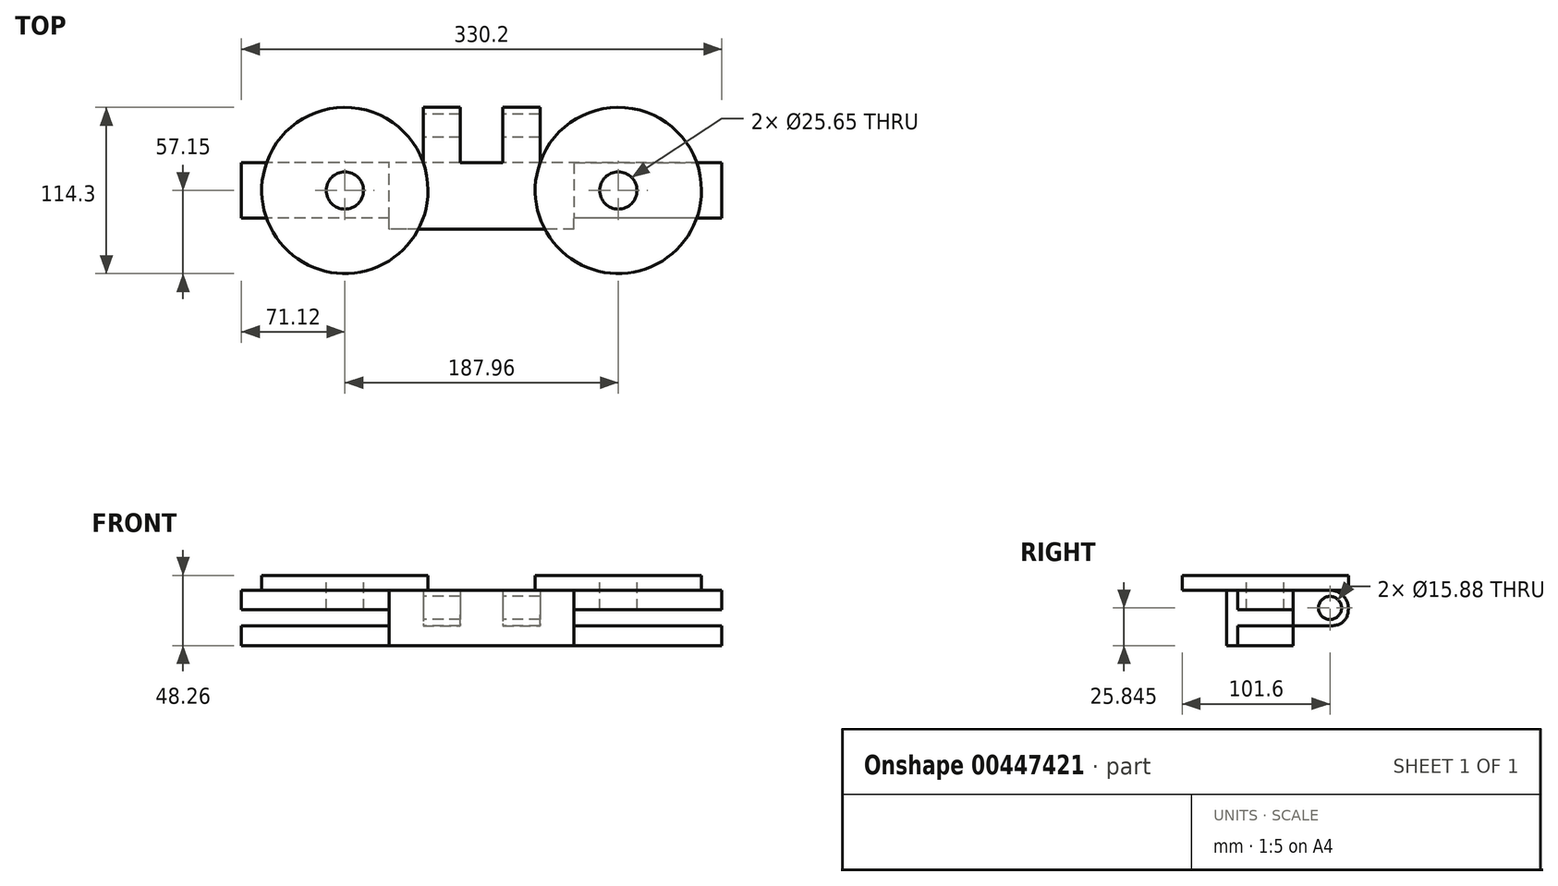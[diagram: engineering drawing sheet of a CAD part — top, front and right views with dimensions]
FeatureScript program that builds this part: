
annotation { "Feature Type Name" : "Feature", "Feature Type Description" : "" }
export const myFeature = defineFeature(function(context is Context, id is Id, definition is map)
    precondition{}
    {
        {
            var Q0;
            Q0=qCreatedBy(makeId("Top.planeOp"),FACE);
            var sketch = newSketch(context, id + "F0", { "sketchPlane" : qUnion([Q0])});
            skLineSegment(sketch, "E0.bottom", {"start": v(165.1, -19.05) * mm, "end": v(-165.1, -19.05) * mm});
            skLineSegment(sketch, "E0.top", {"start": v(165.1, 19.05) * mm, "end": v(-165.1, 19.05) * mm});
            skLineSegment(sketch, "E0.left", {"start": v(165.1, -19.05) * mm, "end": v(165.1, 19.05) * mm});
            skLineSegment(sketch, "E0.right", {"start": v(-165.1, -19.05) * mm, "end": v(-165.1, 19.05) * mm});
            skPoint(sketch, "E0.middle", {"position": v(0, 0) * mm});
            skSolve(sketch);
        }
        {
            var Q0;
            Q0=makeQuery(id+"F0.imprint","IMPRINT",FACE,{"disambiguationData":[TD([[makeQuery(id+"F0.imprint","IMPRINT",EDGE,{"derivedFrom":sQuery(id+"F0.wireOp",EDGE,"E0.bottom")}),-1.0]])]});
            extrude(context, id + "F1", {"entities" : qUnion([Q0]), "depth" : 38.1 * mm});
        }
        {
            var Q0;
            Q0=makeQuery(id+"F1.opExtrude","SWEPT_FACE",FACE,{"disambiguationData":[OSD([sQuery(id+"F0.wireOp",EDGE,"E0.right")])]});
            var sketch = newSketch(context, id + "F2", { "sketchPlane" : qUnion([Q0])});
            skLineSegment(sketch, "E1", {"start": v(0, 38.1) * mm, "end": v(0, 0) * mm});
            skPoint(sketch, "E2", {"position": v(0, 19.05) * mm});
            skLineSegment(sketch, "E3.bottom", {"start": v(19.05, 13.59) * mm, "end": v(-19.05, 13.59) * mm});
            skLineSegment(sketch, "E3.top", {"start": v(19.05, 24.51) * mm, "end": v(-19.05, 24.51) * mm});
            skLineSegment(sketch, "E3.left", {"start": v(19.05, 13.59) * mm, "end": v(19.05, 24.51) * mm});
            skLineSegment(sketch, "E3.right", {"start": v(-19.05, 13.59) * mm, "end": v(-19.05, 24.51) * mm});
            skSolve(sketch);
        }
        {
            var Q0;
            {var subQ5=sQuery(id+"F2.wireOp",EDGE,"E3.left");Q0=makeQuery(id+"F2.imprint","IMPRINT",FACE,{"disambiguationData":[TD([[makeQuery(id+"F2.imprint","IMPRINT",EDGE,{"derivedFrom":subQ5}),-1.0]])]});}
            var Q1;
            {var subQ5=sQuery(id+"F2.wireOp",EDGE,"E3.right");Q1=makeQuery(id+"F2.imprint","IMPRINT",FACE,{"disambiguationData":[TD([[makeQuery(id+"F2.imprint","IMPRINT",EDGE,{"derivedFrom":subQ5}),1.0]])]});}
            extrude(context, id + "F3", {"entities" : qUnion([Q0, Q1]), "operationType" : NewBodyOperationType.REMOVE, "oppositeDirection" : true, "depth" : 101.6 * mm});
        }
        {
            var Q0;
            Q0=makeQuery(id+"F1.opExtrude","SWEPT_FACE",FACE,{"disambiguationData":[OSD([sQuery(id+"F0.wireOp",EDGE,"E0.left")])]});
            var sketch = newSketch(context, id + "F4", { "sketchPlane" : qUnion([Q0])});
            skPoint(sketch, "E4", {"position": v(0, 19.05) * mm});
            skLineSegment(sketch, "E5.bottom", {"start": v(19.05, 13.59) * mm, "end": v(-19.05, 13.59) * mm});
            skLineSegment(sketch, "E5.top", {"start": v(19.05, 24.51) * mm, "end": v(-19.05, 24.51) * mm});
            skLineSegment(sketch, "E5.left", {"start": v(19.05, 13.59) * mm, "end": v(19.05, 24.51) * mm});
            skLineSegment(sketch, "E5.right", {"start": v(-19.05, 13.59) * mm, "end": v(-19.05, 24.51) * mm});
            skLineSegment(sketch, "E6", {"start": v(0, 38.1) * mm, "end": v(0, 0) * mm});
            skPoint(sketch, "E6.endSnap0", {"position": v(0, 0) * mm});
            skSolve(sketch);
        }
        {
            var Q0;
            {var subQ5=sQuery(id+"F4.wireOp",EDGE,"E5.right");Q0=makeQuery(id+"F4.imprint","IMPRINT",FACE,{"disambiguationData":[TD([[makeQuery(id+"F4.imprint","IMPRINT",EDGE,{"derivedFrom":subQ5}),1.0]])]});}
            var Q1;
            {var subQ5=sQuery(id+"F4.wireOp",EDGE,"E5.left");Q1=makeQuery(id+"F4.imprint","IMPRINT",FACE,{"disambiguationData":[TD([[makeQuery(id+"F4.imprint","IMPRINT",EDGE,{"derivedFrom":subQ5}),-1.0]])]});}
            extrude(context, id + "F5", {"entities" : qUnion([Q0, Q1]), "operationType" : NewBodyOperationType.REMOVE, "oppositeDirection" : true, "depth" : 101.6 * mm});
        }
        {
            var Q0;
            Q0=makeQuery(id+"F1.opExtrude","CAP_FACE",FACE,{"disambiguationData":[OSD([sQuery(id+"F0.wireOp",EDGE,"E0.bottom"),sQuery(id+"F0.wireOp",EDGE,"E0.top"),sQuery(id+"F0.wireOp",EDGE,"E0.left"),sQuery(id+"F0.wireOp",EDGE,"E0.right")])],"isStart":false});
            var sketch = newSketch(context, id + "F6", { "sketchPlane" : qUnion([Q0])});
            skLineSegment(sketch, "E7", {"start": v(-93.98, -19.05) * mm, "end": v(-93.98, 19.05) * mm});
            skPoint(sketch, "E8", {"position": v(-93.98, 0) * mm});
            skCircle(sketch, "E9", {"center": v(-93.98, 0) * mm, "radius": 12.83 * mm});
            skLineSegment(sketch, "E10", {"start": v(93.98, 19.05) * mm, "end": v(93.98, -19.05) * mm});
            skPoint(sketch, "E11", {"position": v(93.98, 0) * mm});
            skCircle(sketch, "E12", {"center": v(93.98, 0) * mm, "radius": 12.83 * mm});
            skCircle(sketch, "E13", {"center": v(93.98, 0) * mm, "radius": 57.15 * mm});
            skCircle(sketch, "E14", {"center": v(93.98, 0) * mm, "radius": 25.4 * mm});
            skCircle(sketch, "E15", {"center": v(-93.98, 0) * mm, "radius": 57.15 * mm});
            skSolve(sketch);
        }
        {
            var Q0;
            {var subQ0=sQuery(id+"F6.wireOp",EDGE,"E9");var subQ1=sQuery(id+"F6.wireOp",EDGE,"E7");var subQ2=makeQuery(id+"F6.imprint","INTERSECT",VERTEX,{"disambiguationData":[OD(0.0)],"derivedFrom":[subQ1,subQ0]});Q0=makeQuery(id+"F6.imprint","IMPRINT",FACE,{"disambiguationData":[TD([[makeQuery(id+"F6.imprint","IMPRINT",EDGE,{"disambiguationData":[TD([[subQ2,-1.0]])],"derivedFrom":subQ1}),-1.0]])]});}
            var Q1;
            {var subQ0=sQuery(id+"F6.wireOp",EDGE,"E9");var subQ1=sQuery(id+"F6.wireOp",EDGE,"E7");var subQ2=makeQuery(id+"F6.imprint","INTERSECT",VERTEX,{"disambiguationData":[OD(0.0)],"derivedFrom":[subQ1,subQ0]});Q1=makeQuery(id+"F6.imprint","IMPRINT",FACE,{"disambiguationData":[TD([[makeQuery(id+"F6.imprint","IMPRINT",EDGE,{"disambiguationData":[TD([[subQ2,-1.0]])],"derivedFrom":subQ1}),1.0]])]});}
            var Q2;
            {var subQ0=sQuery(id+"F6.wireOp",EDGE,"E12");var subQ1=sQuery(id+"F6.wireOp",EDGE,"E10");var subQ2=makeQuery(id+"F6.imprint","INTERSECT",VERTEX,{"disambiguationData":[OD(0.0)],"derivedFrom":[subQ1,subQ0]});Q2=makeQuery(id+"F6.imprint","IMPRINT",FACE,{"disambiguationData":[TD([[makeQuery(id+"F6.imprint","IMPRINT",EDGE,{"disambiguationData":[TD([[subQ2,-1.0]])],"derivedFrom":subQ1}),-1.0]])]});}
            var Q3;
            {var subQ0=sQuery(id+"F6.wireOp",EDGE,"E12");var subQ1=sQuery(id+"F6.wireOp",EDGE,"E10");var subQ2=makeQuery(id+"F6.imprint","INTERSECT",VERTEX,{"disambiguationData":[OD(0.0)],"derivedFrom":[subQ1,subQ0]});Q3=makeQuery(id+"F6.imprint","IMPRINT",FACE,{"disambiguationData":[TD([[makeQuery(id+"F6.imprint","IMPRINT",EDGE,{"disambiguationData":[TD([[subQ2,-1.0]])],"derivedFrom":subQ1}),1.0]])]});}
            extrude(context, id + "F7", {"entities" : qUnion([Q0, Q1, Q2, Q3]), "operationType" : NewBodyOperationType.REMOVE, "oppositeDirection" : true, "depth" : 22.86 * mm});
        }
        {
            var Q0;
            {var subQ0=sQuery(id+"F6.wireOp",EDGE,"E14");var subQ1=makeQuery(id+"F1.opExtrude","CAP_EDGE",EDGE,{"disambiguationData":[OSD([sQuery(id+"F0.wireOp",EDGE,"E0.top")])],"isStart":false});var subQ2=makeQuery(id+"F6.imprint","INTERSECT",VERTEX,{"disambiguationData":[OD(0.0)],"derivedFrom":[subQ1,subQ0]});Q0=makeQuery(id+"F6.imprint","IMPRINT",FACE,{"disambiguationData":[TD([[makeQuery(id+"F6.imprint","IMPRINT",EDGE,{"disambiguationData":[TD([[subQ2,1.0]])],"derivedFrom":subQ0}),1.0]])]});}
            var Q1;
            {var subQ0=sQuery(id+"F6.wireOp",EDGE,"E13");var subQ1=makeQuery(id+"F1.opExtrude","CAP_EDGE",EDGE,{"disambiguationData":[OSD([sQuery(id+"F0.wireOp",EDGE,"E0.top")])],"isStart":false});var subQ2=makeQuery(id+"F6.imprint","INTERSECT",VERTEX,{"disambiguationData":[OD(1.0)],"derivedFrom":[subQ1,subQ0]});Q1=makeQuery(id+"F6.imprint","IMPRINT",FACE,{"disambiguationData":[TD([[makeQuery(id+"F6.imprint","IMPRINT",EDGE,{"disambiguationData":[TD([[subQ2,1.0]])],"derivedFrom":subQ0}),1.0]])]});}
            var Q2;
            {var subQ0=sQuery(id+"F6.wireOp",EDGE,"E13");var subQ1=makeQuery(id+"F1.opExtrude","CAP_EDGE",EDGE,{"disambiguationData":[OSD([sQuery(id+"F0.wireOp",EDGE,"E0.top")])],"isStart":false});var subQ2=makeQuery(id+"F6.imprint","INTERSECT",VERTEX,{"disambiguationData":[OD(0.0)],"derivedFrom":[subQ1,subQ0]});Q2=makeQuery(id+"F6.imprint","IMPRINT",FACE,{"disambiguationData":[TD([[makeQuery(id+"F6.imprint","IMPRINT",EDGE,{"disambiguationData":[TD([[subQ2,1.0]])],"derivedFrom":subQ0}),1.0]])]});}
            var Q3;
            {var subQ1=sQuery(id+"F6.wireOp",EDGE,"E10");var subQ4=makeQuery(id+"F1.opExtrude","CAP_EDGE",EDGE,{"disambiguationData":[OSD([sQuery(id+"F0.wireOp",EDGE,"E0.top")])],"isStart":false});var subQ5=makeQuery(id+"F6.imprint","INTERSECT",VERTEX,{"derivedFrom":[subQ4,subQ1]});Q3=makeQuery(id+"F6.imprint","IMPRINT",FACE,{"disambiguationData":[TD([[makeQuery(id+"F6.imprint","IMPRINT",EDGE,{"disambiguationData":[TD([[subQ5,-1.0]])],"derivedFrom":subQ1}),-1.0]])]});}
            var Q4;
            {var subQ1=sQuery(id+"F6.wireOp",EDGE,"E10");var subQ4=makeQuery(id+"F1.opExtrude","CAP_EDGE",EDGE,{"disambiguationData":[OSD([sQuery(id+"F0.wireOp",EDGE,"E0.top")])],"isStart":false});var subQ5=makeQuery(id+"F6.imprint","INTERSECT",VERTEX,{"derivedFrom":[subQ4,subQ1]});Q4=makeQuery(id+"F6.imprint","IMPRINT",FACE,{"disambiguationData":[TD([[makeQuery(id+"F6.imprint","IMPRINT",EDGE,{"disambiguationData":[TD([[subQ5,-1.0]])],"derivedFrom":subQ1}),1.0]])]});}
            var Q5;
            {var subQ0=sQuery(id+"F6.wireOp",EDGE,"E13");var subQ1=makeQuery(id+"F1.opExtrude","CAP_EDGE",EDGE,{"disambiguationData":[OSD([sQuery(id+"F0.wireOp",EDGE,"E0.top")])],"isStart":false});var subQ2=makeQuery(id+"F6.imprint","INTERSECT",VERTEX,{"disambiguationData":[OD(0.0)],"derivedFrom":[subQ1,subQ0]});Q5=makeQuery(id+"F6.imprint","IMPRINT",FACE,{"disambiguationData":[TD([[makeQuery(id+"F6.imprint","IMPRINT",EDGE,{"disambiguationData":[TD([[subQ2,-1.0]])],"derivedFrom":subQ0}),1.0]])]});}
            var Q6;
            {var subQ0=sQuery(id+"F6.wireOp",EDGE,"E13");var subQ1=makeQuery(id+"F1.opExtrude","CAP_EDGE",EDGE,{"disambiguationData":[OSD([sQuery(id+"F0.wireOp",EDGE,"E0.bottom")])],"isStart":false});var subQ2=makeQuery(id+"F6.imprint","INTERSECT",VERTEX,{"disambiguationData":[OD(0.0)],"derivedFrom":[subQ1,subQ0]});Q6=makeQuery(id+"F6.imprint","IMPRINT",FACE,{"disambiguationData":[TD([[makeQuery(id+"F6.imprint","IMPRINT",EDGE,{"disambiguationData":[TD([[subQ2,-1.0]])],"derivedFrom":subQ0}),1.0]])]});}
            var Q7;
            {var subQ0=sQuery(id+"F6.wireOp",EDGE,"E14");var subQ1=makeQuery(id+"F1.opExtrude","CAP_EDGE",EDGE,{"disambiguationData":[OSD([sQuery(id+"F0.wireOp",EDGE,"E0.bottom")])],"isStart":false});var subQ2=makeQuery(id+"F6.imprint","INTERSECT",VERTEX,{"disambiguationData":[OD(0.0)],"derivedFrom":[subQ1,subQ0]});Q7=makeQuery(id+"F6.imprint","IMPRINT",FACE,{"disambiguationData":[TD([[makeQuery(id+"F6.imprint","IMPRINT",EDGE,{"disambiguationData":[TD([[subQ2,-1.0]])],"derivedFrom":subQ0}),1.0]])]});}
            var Q8;
            {var subQ3=makeQuery(id+"F1.opExtrude","CAP_EDGE",EDGE,{"disambiguationData":[OSD([sQuery(id+"F0.wireOp",EDGE,"E0.bottom")])],"isStart":false});var subQ6=sQuery(id+"F6.wireOp",EDGE,"E7");var subQ10=makeQuery(id+"F6.imprint","INTERSECT",VERTEX,{"derivedFrom":[subQ3,subQ6]});Q8=makeQuery(id+"F6.imprint","IMPRINT",FACE,{"disambiguationData":[TD([[makeQuery(id+"F6.imprint","IMPRINT",EDGE,{"disambiguationData":[TD([[subQ10,-1.0]])],"derivedFrom":subQ6}),-1.0]])]});}
            var Q9;
            {var subQ3=makeQuery(id+"F1.opExtrude","CAP_EDGE",EDGE,{"disambiguationData":[OSD([sQuery(id+"F0.wireOp",EDGE,"E0.bottom")])],"isStart":false});var subQ5=sQuery(id+"F6.wireOp",EDGE,"E7");var subQ6=makeQuery(id+"F6.imprint","INTERSECT",VERTEX,{"derivedFrom":[subQ3,subQ5]});Q9=makeQuery(id+"F6.imprint","IMPRINT",FACE,{"disambiguationData":[TD([[makeQuery(id+"F6.imprint","IMPRINT",EDGE,{"disambiguationData":[TD([[subQ6,-1.0]])],"derivedFrom":subQ5}),1.0]])]});}
            var Q10;
            {var subQ0=sQuery(id+"F6.wireOp",EDGE,"E15");var subQ1=makeQuery(id+"F1.opExtrude","CAP_EDGE",EDGE,{"disambiguationData":[OSD([sQuery(id+"F0.wireOp",EDGE,"E0.bottom")])],"isStart":false});var subQ2=makeQuery(id+"F6.imprint","INTERSECT",VERTEX,{"disambiguationData":[OD(0.0)],"derivedFrom":[subQ1,subQ0]});Q10=makeQuery(id+"F6.imprint","IMPRINT",FACE,{"disambiguationData":[TD([[makeQuery(id+"F6.imprint","IMPRINT",EDGE,{"disambiguationData":[TD([[subQ2,-1.0]])],"derivedFrom":subQ0}),1.0]])]});}
            var Q11;
            {var subQ0=sQuery(id+"F6.wireOp",EDGE,"E15");var subQ1=makeQuery(id+"F1.opExtrude","CAP_EDGE",EDGE,{"disambiguationData":[OSD([sQuery(id+"F0.wireOp",EDGE,"E0.top")])],"isStart":false});var subQ2=makeQuery(id+"F6.imprint","INTERSECT",VERTEX,{"disambiguationData":[OD(0.0)],"derivedFrom":[subQ1,subQ0]});Q11=makeQuery(id+"F6.imprint","IMPRINT",FACE,{"disambiguationData":[TD([[makeQuery(id+"F6.imprint","IMPRINT",EDGE,{"disambiguationData":[TD([[subQ2,1.0]])],"derivedFrom":subQ0}),1.0]])]});}
            extrude(context, id + "F8", {"entities" : qUnion([Q0, Q1, Q2, Q3, Q4, Q5, Q6, Q7, Q8, Q9, Q10, Q11]), "operationType" : NewBodyOperationType.ADD, "depth" : 10.16 * mm});
        }
        {
            var Q0;
            Q0=makeQuery(id+"F1.opExtrude","SWEPT_FACE",FACE,{"disambiguationData":[OSD([sQuery(id+"F0.wireOp",EDGE,"E0.bottom")])]});
            var sketch = newSketch(context, id + "F9", { "sketchPlane" : qUnion([Q0])});
            skPoint(sketch, "E16.endSnap0", {"position": v(-63.5, 19.05) * mm});
            skPoint(sketch, "E17", {"position": v(78.24, 25.4) * mm});
            skLineSegment(sketch, "E18.top", {"start": v(373.59, 38.1) * mm, "end": v(13.55, 38.1) * mm});
            skLineSegment(sketch, "E18.left", {"start": v(63.5, 19.94) * mm, "end": v(63.5, 30.86) * mm});
            skLineSegment(sketch, "E18.right", {"start": v(-63.5, 19.94) * mm, "end": v(-63.5, 30.86) * mm});
            skLineSegment(sketch, "E19", {"start": v(0, 38.1) * mm, "end": v(0, 0) * mm});
            skLineSegment(sketch, "E20.bottom", {"start": v(63.5, 0) * mm, "end": v(-63.5, 0) * mm});
            skLineSegment(sketch, "E20.top", {"start": v(63.5, 38.1) * mm, "end": v(-63.5, 38.1) * mm});
            skLineSegment(sketch, "E20.left", {"start": v(63.5, 0) * mm, "end": v(63.5, 38.1) * mm});
            skLineSegment(sketch, "E20.right", {"start": v(-63.5, 0) * mm, "end": v(-63.5, 38.1) * mm});
            skPoint(sketch, "E20.middle", {"position": v(0, 19.05) * mm});
            skSolve(sketch);
        }
        {
            var Q0;
            {var subQ1=sQuery(id+"F9.wireOp",EDGE,"I8A0hCDH-xshG-kS3o-E5Fb-7KzM2OnlTiHC");Q0=makeQuery(id+"F9.imprint","IMPRINT",FACE,{"disambiguationData":[TD([[makeQuery(id+"F9.imprint","IMPRINT",EDGE,{"derivedFrom":subQ1}),-1.0]])]});}
            var Q1;
            {var subQ1=sQuery(id+"F9.wireOp",EDGE,"I8A0hCDH-xshG-kS3o-E5Fb-7KzM2OnlTiHC");Q1=makeQuery(id+"F9.imprint","IMPRINT",FACE,{"disambiguationData":[TD([[makeQuery(id+"F9.imprint","IMPRINT",EDGE,{"derivedFrom":subQ1}),1.0]])]});}
            var Q2;
            {var subQ6=sQuery(id+"F9.wireOp",EDGE,"E19");Q2=makeQuery(id+"F9.imprint","IMPRINT",FACE,{"disambiguationData":[TD([[makeQuery(id+"F9.imprint","IMPRINT",EDGE,{"derivedFrom":subQ6}),-1.0]])]});}
            var Q3;
            {var subQ2=sQuery(id+"F9.wireOp",EDGE,"E19");Q3=makeQuery(id+"F9.imprint","IMPRINT",FACE,{"disambiguationData":[TD([[makeQuery(id+"F9.imprint","IMPRINT",EDGE,{"derivedFrom":subQ2}),1.0]])]});}
            extrude(context, id + "F10", {"entities" : qUnion([Q0, Q1, Q2, Q3]), "operationType" : NewBodyOperationType.ADD, "depth" : 7.62 * mm});
        }
        {
            var Q0;
            Q0=makeQuery(id+"F1.opExtrude","SWEPT_FACE",FACE,{"disambiguationData":[OSD([sQuery(id+"F0.wireOp",EDGE,"E0.top")])]});
            var sketch = newSketch(context, id + "F11", { "sketchPlane" : qUnion([Q0])});
            skLineSegment(sketch, "E21", {"start": v(0, 0) * mm, "end": v(0, 38.1) * mm});
            skPoint(sketch, "E22", {"position": v(0, 19.05) * mm});
            skLineSegment(sketch, "E23.bottom", {"start": v(-63.5, 24.51) * mm, "end": v(63.5, 24.51) * mm});
            skLineSegment(sketch, "E23.top", {"start": v(-63.5, 13.59) * mm, "end": v(63.5, 13.59) * mm});
            skLineSegment(sketch, "E23.left", {"start": v(-63.5, 24.51) * mm, "end": v(-63.5, 13.59) * mm});
            skLineSegment(sketch, "E23.right", {"start": v(63.5, 24.51) * mm, "end": v(63.5, 13.59) * mm});
            skLineSegment(sketch, "E24", {"start": v(-63.5, 38.1) * mm, "end": v(-63.5, 24.51) * mm});
            skPoint(sketch, "E24.startSnap0", {"position": v(-63.5, 19.05) * mm});
            skLineSegment(sketch, "E25", {"start": v(63.5, 24.51) * mm, "end": v(63.5, 38.1) * mm});
            skLineSegment(sketch, "E26", {"start": v(63.5, 38.1) * mm, "end": v(0, 38.1) * mm});
            skLineSegment(sketch, "E27", {"start": v(0, 38.1) * mm, "end": v(-63.5, 38.1) * mm});
            skLineSegment(sketch, "E28", {"start": v(0, 0) * mm, "end": v(63.5, 0) * mm});
            skLineSegment(sketch, "E29", {"start": v(63.5, 0) * mm, "end": v(63.5, 13.59) * mm});
            skLineSegment(sketch, "E30", {"start": v(-63.5, 13.59) * mm, "end": v(-63.5, 0) * mm});
            skLineSegment(sketch, "E31", {"start": v(-63.5, 0) * mm, "end": v(0, 0) * mm});
            skLineSegment(sketch, "E32", {"start": v(-40.1, 38.1) * mm, "end": v(-40.1, 0) * mm});
            skLineSegment(sketch, "E33", {"start": v(40.1, 38.1) * mm, "end": v(40.1, 0) * mm});
            skLineSegment(sketch, "E34", {"start": v(14.7, 38.1) * mm, "end": v(14.7, 0) * mm});
            skLineSegment(sketch, "E35", {"start": v(-14.7, 38.1) * mm, "end": v(-14.7, 0) * mm});
            skSolve(sketch);
        }
        {
            var Q0;
            {var subQ0=sQuery(id+"F11.wireOp",EDGE,"E32");var subQ1=sQuery(id+"F11.wireOp",EDGE,"E23.bottom");var subQ2=makeQuery(id+"F11.imprint","INTERSECT",VERTEX,{"derivedFrom":[subQ1,subQ0]});Q0=makeQuery(id+"F11.imprint","IMPRINT",FACE,{"disambiguationData":[TD([[makeQuery(id+"F11.imprint","IMPRINT",EDGE,{"disambiguationData":[TD([[subQ2,-1.0]])],"derivedFrom":subQ1}),1.0]])]});}
            var Q1;
            {var subQ0=sQuery(id+"F11.wireOp",EDGE,"E32");var subQ1=sQuery(id+"F11.wireOp",EDGE,"E23.bottom");var subQ2=makeQuery(id+"F11.imprint","INTERSECT",VERTEX,{"derivedFrom":[subQ1,subQ0]});Q1=makeQuery(id+"F11.imprint","IMPRINT",FACE,{"disambiguationData":[TD([[makeQuery(id+"F11.imprint","IMPRINT",EDGE,{"disambiguationData":[TD([[subQ2,-1.0]])],"derivedFrom":subQ1}),-1.0]])]});}
            var Q2;
            {var subQ0=sQuery(id+"F11.wireOp",EDGE,"E34");var subQ1=sQuery(id+"F11.wireOp",EDGE,"E23.bottom");var subQ2=makeQuery(id+"F11.imprint","INTERSECT",VERTEX,{"derivedFrom":[subQ1,subQ0]});Q2=makeQuery(id+"F11.imprint","IMPRINT",FACE,{"disambiguationData":[TD([[makeQuery(id+"F11.imprint","IMPRINT",EDGE,{"disambiguationData":[TD([[subQ2,-1.0]])],"derivedFrom":subQ1}),-1.0]])]});}
            var Q3;
            {var subQ0=sQuery(id+"F11.wireOp",EDGE,"E34");var subQ1=sQuery(id+"F11.wireOp",EDGE,"E23.bottom");var subQ2=makeQuery(id+"F11.imprint","INTERSECT",VERTEX,{"derivedFrom":[subQ1,subQ0]});Q3=makeQuery(id+"F11.imprint","IMPRINT",FACE,{"disambiguationData":[TD([[makeQuery(id+"F11.imprint","IMPRINT",EDGE,{"disambiguationData":[TD([[subQ2,-1.0]])],"derivedFrom":subQ1}),1.0]])]});}
            extrude(context, id + "F12", {"entities" : qUnion([Q0, Q1, Q2, Q3]), "operationType" : NewBodyOperationType.ADD, "depth" : 38.1 * mm});
        }
        {
            var Q0;
            {var subQ0=sQuery(id+"F11.wireOp",EDGE,"E23.top");Q0=makeQuery(id+"F12.opExtrude","CAP_EDGE",EDGE,{"disambiguationData":[OSD([subQ0]),TDD([makeQuery(id+"F11.imprint","IMPRINT",EDGE,{"disambiguationData":[TD([[makeQuery(id+"F11.imprint","INTERSECT",VERTEX,{"derivedFrom":[subQ0,sQuery(id+"F11.wireOp",EDGE,"E34")]}),-1.0]])],"derivedFrom":subQ0})])],"isStart":false});}
            var Q1;
            {var subQ0=sQuery(id+"F11.wireOp",EDGE,"E23.top");Q1=makeQuery(id+"F12.opExtrude","CAP_EDGE",EDGE,{"disambiguationData":[OSD([subQ0]),TDD([makeQuery(id+"F11.imprint","IMPRINT",EDGE,{"disambiguationData":[TD([[makeQuery(id+"F11.imprint","INTERSECT",VERTEX,{"derivedFrom":[subQ0,sQuery(id+"F11.wireOp",EDGE,"E32")]}),-1.0]])],"derivedFrom":subQ0})])],"isStart":false});}
            fillet(context, id + "F13", {"entities" : qUnion([Q0, Q1]), "radius" : 12.7 * mm, "tangentPropagation" : true, "rho" : 0.5, "crossSection" : FilletCrossSection.CONIC, "allowEdgeOverflow" : false});
        }
        {
            var Q0;
            Q0=makeQuery(id+"F12.opExtrude","CAP_EDGE",EDGE,{"disambiguationData":[OSD([sQuery(id+"F11.wireOp",EDGE,"E27")])],"isStart":false});
            var Q1;
            Q1=makeQuery(id+"F12.opExtrude","CAP_EDGE",EDGE,{"disambiguationData":[OSD([sQuery(id+"F11.wireOp",EDGE,"E26")])],"isStart":false});
            fillet(context, id + "F14", {"entities" : qUnion([Q0, Q1]), "radius" : 12.7 * mm, "tangentPropagation" : true, "allowEdgeOverflow" : false});
        }
        {
            var Q0;
            Q0=makeQuery(id+"F12.opExtrude","SWEPT_FACE",FACE,{"disambiguationData":[OSD([sQuery(id+"F11.wireOp",EDGE,"E33")])]});
            var sketch = newSketch(context, id + "F15", { "sketchPlane" : qUnion([Q0])});
            skLineSegment(sketch, "E36", {"start": v(-19.05, 25.84) * mm, "end": v(-68.87, 25.84) * mm});
            skCircle(sketch, "E37", {"center": v(-44.45, 25.84) * mm, "radius": 7.94 * mm});
            skSolve(sketch);
        }
        {
            var Q0;
            {var subQ0=sQuery(id+"F15.wireOp",EDGE,"E37");var subQ1=sQuery(id+"F15.wireOp",EDGE,"E36");var subQ2=makeQuery(id+"F15.imprint","INTERSECT",VERTEX,{"disambiguationData":[OD(0.0)],"derivedFrom":[subQ1,subQ0]});Q0=makeQuery(id+"F15.imprint","IMPRINT",FACE,{"disambiguationData":[TD([[makeQuery(id+"F15.imprint","IMPRINT",EDGE,{"disambiguationData":[TD([[subQ2,-1.0]])],"derivedFrom":subQ1}),1.0]])]});}
            var Q1;
            {var subQ0=sQuery(id+"F15.wireOp",EDGE,"E37");var subQ1=sQuery(id+"F15.wireOp",EDGE,"E36");var subQ2=makeQuery(id+"F15.imprint","INTERSECT",VERTEX,{"disambiguationData":[OD(0.0)],"derivedFrom":[subQ1,subQ0]});Q1=makeQuery(id+"F15.imprint","IMPRINT",FACE,{"disambiguationData":[TD([[makeQuery(id+"F15.imprint","IMPRINT",EDGE,{"disambiguationData":[TD([[subQ2,-1.0]])],"derivedFrom":subQ1}),-1.0]])]});}
            extrude(context, id + "F16", {"entities" : qUnion([Q0, Q1]), "operationType" : NewBodyOperationType.REMOVE, "oppositeDirection" : true, "depth" : 101.6 * mm});
        }
    });
